# Revit family: Oak
name_source: partatom
category: Мебель
revit_build: Autodesk Revit 2017 (Build: 20160225_1515(x64)
units: mm (PartAtom-declared; Revit-internal decimal feet)

## family parameters
Всегда вертикально = Да
Заголовок OmniClass = General Furniture and Specialties
На основе рабочей плоскости = Нет
Номер OmniClass = 23.40.20.00
Общий = Нет
При загрузке вырезать с полостями = Нет
Точка расчета площади = Нет

## types (4) — shared parameters
Material = Skandiform Wood Oak
Изготовитель = Skandiform AB
Ключевая пометка = XBE.1
Описание = Table in solid ash or oak, turned legs

## per-type parameters (varying)
| type | Length | Table Leg | URL | Width | Комментарии к типоразмеру |
| HB-500 | 2400 мм | HB-500-Legrfa | http://file-system.ru | 740 мм | Created by Astacus AB
Created by Astacus AB |
| HB-501 | 3150 мм | HB-501-Legrfa | http://www.biminfo.se | 740 мм | Created by Astacus AB |
| HB-502 | 2400 мм | HB-502-Legrfa | http://www.biminfo.se | 850 мм | Created by Astacus AB |
| HB-505 | 1800 мм | HB-505-Legrfa | http://www.biminfo.se | 600 мм | Created by Astacus AB |

note: column(s) folded — value = type name in every type: Группа модели

## geometry (parser evidence)
native form markers: Blend x12, Sweep x12
no freeform markers — native parametric forms only
